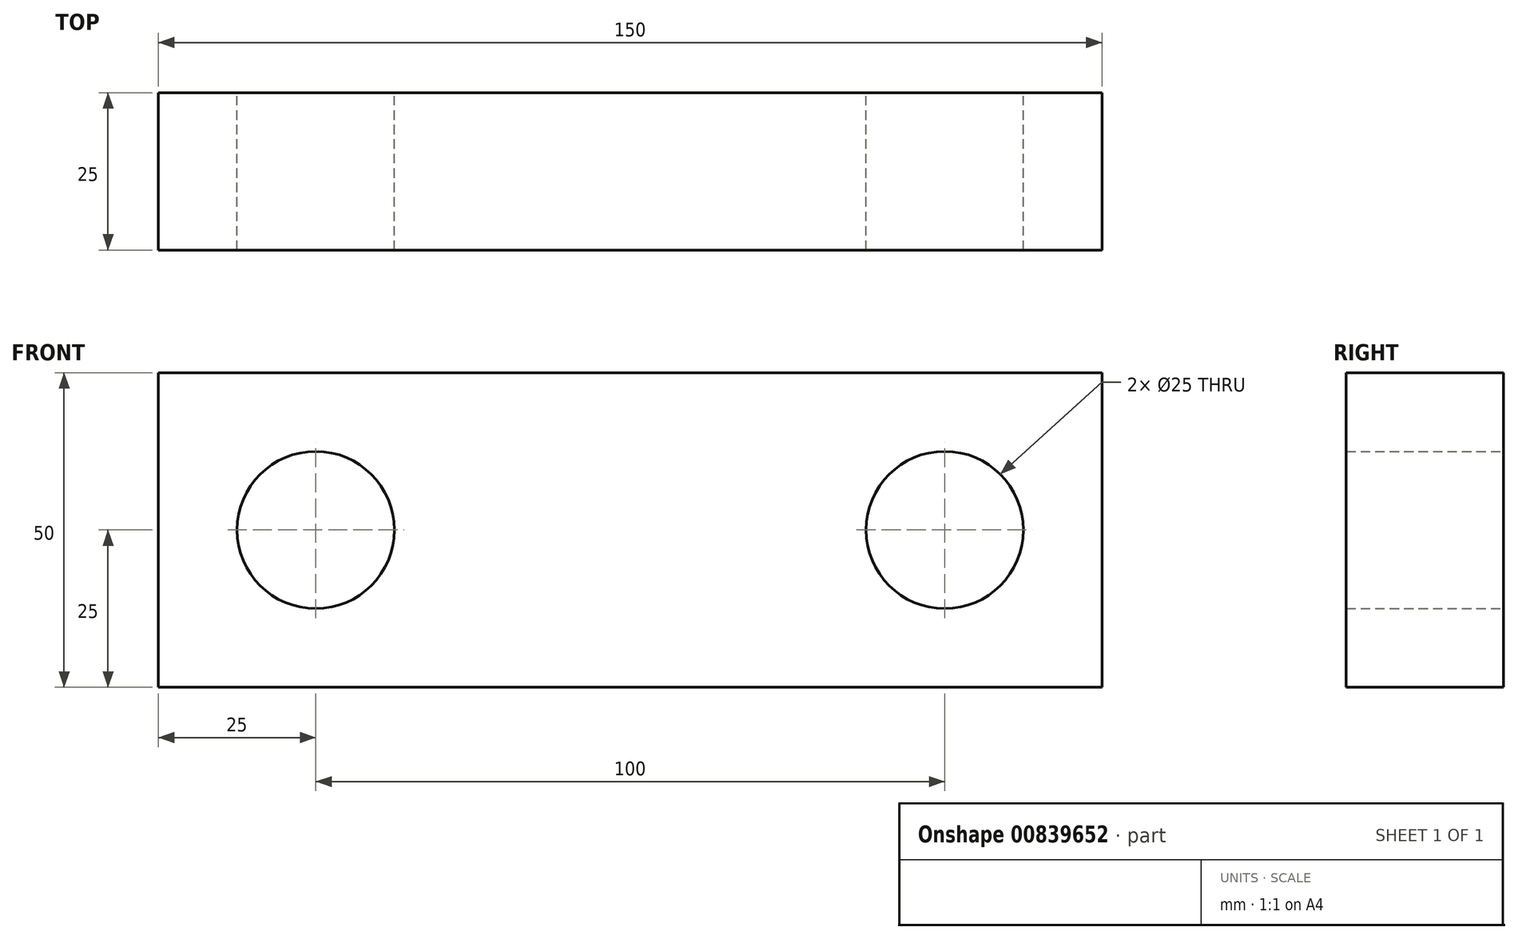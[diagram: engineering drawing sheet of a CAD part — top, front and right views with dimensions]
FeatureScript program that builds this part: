
annotation { "Feature Type Name" : "Feature", "Feature Type Description" : "" }
export const myFeature = defineFeature(function(context is Context, id is Id, definition is map)
    precondition{}
    {
        {
            var Q0;
            Q0=qCreatedBy(makeId("Front.planeOp"),FACE);
            var sketch = newSketch(context, id + "F0", { "sketchPlane" : qUnion([Q0])});
            skCircle(sketch, "E0", {"center": v(-50, 0) * mm, "radius": 12.5 * mm});
            skCircle(sketch, "E1", {"center": v(50, 0) * mm, "radius": 12.5 * mm});
            skLineSegment(sketch, "E2", {"start": v(-50, 0) * mm, "end": v(50, 0) * mm, "construction": true});
            skPoint(sketch, "E3", {"position": v(0, 0) * mm});
            skLineSegment(sketch, "E4.bottom", {"start": v(-75, 25) * mm, "end": v(75, 25) * mm});
            skLineSegment(sketch, "E4.top", {"start": v(-75, -25) * mm, "end": v(75, -25) * mm});
            skLineSegment(sketch, "E4.left", {"start": v(-75, 25) * mm, "end": v(-75, -25) * mm});
            skLineSegment(sketch, "E4.right", {"start": v(75, 25) * mm, "end": v(75, -25) * mm});
            skLineSegment(sketch, "E5", {"start": v(50, 0) * mm, "end": v(75, 25) * mm, "construction": true});
            skLineSegment(sketch, "E6", {"start": v(50, 0) * mm, "end": v(75, -25) * mm, "construction": true});
            skLineSegment(sketch, "E7", {"start": v(-50, 0) * mm, "end": v(-75, 25) * mm, "construction": true});
            skLineSegment(sketch, "E8", {"start": v(-50, 0) * mm, "end": v(-75, -25) * mm, "construction": true});
            skSolve(sketch);
        }
        {
            var Q0;
            Q0=makeQuery(id+"F0.imprint","IMPRINT",FACE,{"disambiguationData":[TD([[makeQuery(id+"F0.imprint","IMPRINT",EDGE,{"derivedFrom":sQuery(id+"F0.wireOp",EDGE,"E0")}),-1.0]])]});
            extrude(context, id + "F1", {"entities" : qUnion([Q0]), "depth" : 25 * mm, "offsetDistance" : 25 * mm});
        }
    });
